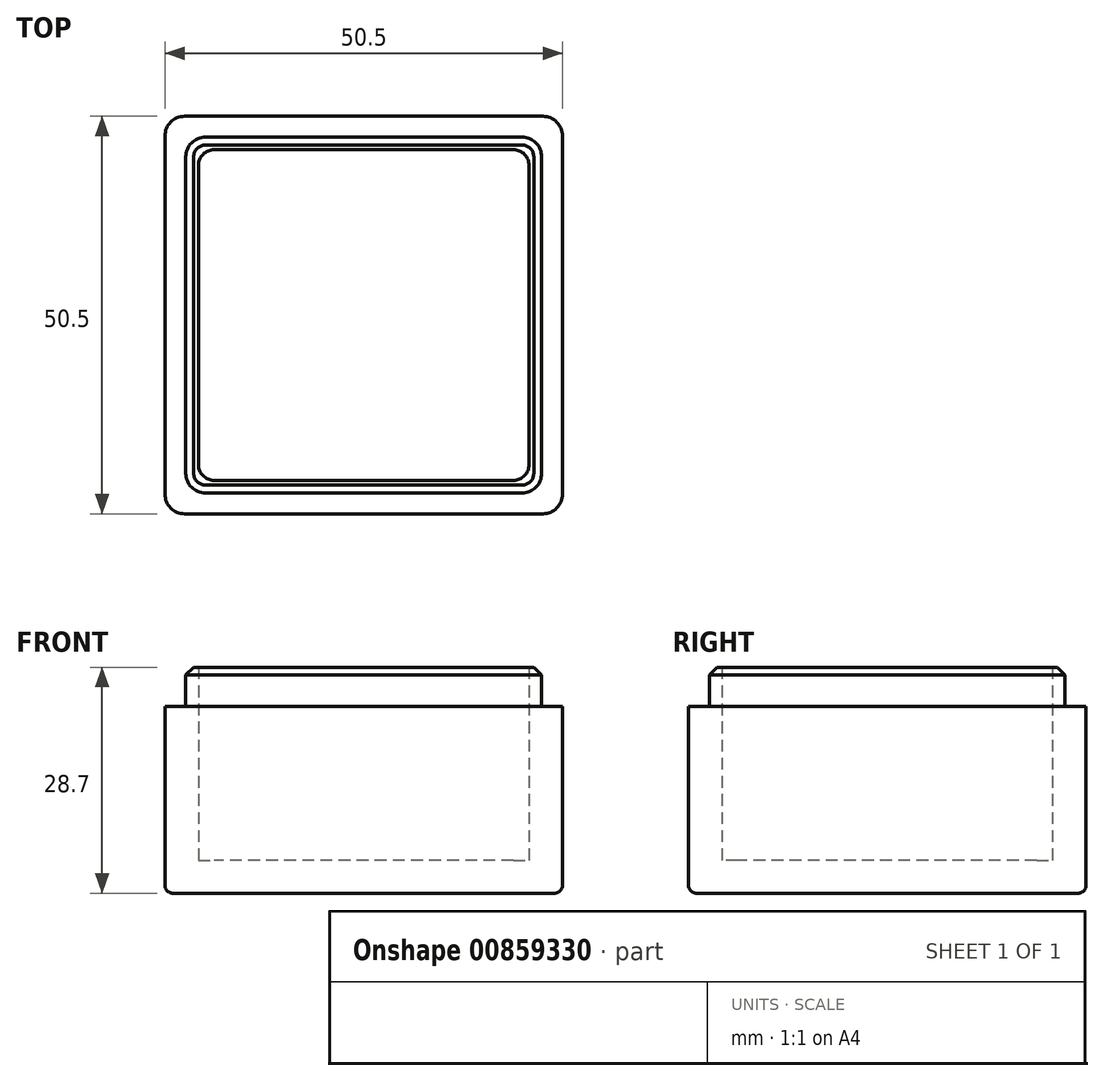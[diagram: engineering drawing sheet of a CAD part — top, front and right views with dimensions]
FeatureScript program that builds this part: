
annotation { "Feature Type Name" : "Feature", "Feature Type Description" : "" }
export const myFeature = defineFeature(function(context is Context, id is Id, definition is map)
    precondition{}
    {
        {
            var Q0;
            Q0=qCreatedBy(makeId("Top.planeOp"),FACE);
            var sketch = newSketch(context, id + "F0", { "sketchPlane" : qUnion([Q0])});
            skLineSegment(sketch, "E0.bottom", {"start": v(25.25, 25.25) * mm, "end": v(-25.25, 25.25) * mm});
            skLineSegment(sketch, "E0.top", {"start": v(25.25, -25.25) * mm, "end": v(-25.25, -25.25) * mm});
            skLineSegment(sketch, "E0.left", {"start": v(25.25, 25.25) * mm, "end": v(25.25, -25.25) * mm});
            skLineSegment(sketch, "E0.right", {"start": v(-25.25, 25.25) * mm, "end": v(-25.25, -25.25) * mm});
            skPoint(sketch, "E0.middle", {"position": v(0, 0) * mm});
            skSolve(sketch);
        }
        {
            var Q0;
            Q0=qSketchRegion(id+"F0",true);
            extrude(context, id + "F1", {"entities" : qUnion([Q0]), "depth" : (2 + 20 + 1.7) * mm, "offsetDistance" : 25 * mm});
        }
        {
            var Q0;
            Q0=makeQuery(id+"F1.opExtrude","CAP_FACE",FACE,{"disambiguationData":[OSD([sQuery(id+"F0.wireOp",EDGE,"E0.bottom"),sQuery(id+"F0.wireOp",EDGE,"E0.top"),sQuery(id+"F0.wireOp",EDGE,"E0.left"),sQuery(id+"F0.wireOp",EDGE,"E0.right")])],"isStart":false});
            var sketch = newSketch(context, id + "F2", { "sketchPlane" : qUnion([Q0])});
            skLineSegment(sketch, "E1.bottom", {"start": v(22.6, 22.6) * mm, "end": v(-22.6, 22.6) * mm});
            skLineSegment(sketch, "E1.top", {"start": v(22.6, -22.6) * mm, "end": v(-22.6, -22.6) * mm});
            skLineSegment(sketch, "E1.left", {"start": v(22.6, 22.6) * mm, "end": v(22.6, -22.6) * mm});
            skLineSegment(sketch, "E1.right", {"start": v(-22.6, 22.6) * mm, "end": v(-22.6, -22.6) * mm});
            skPoint(sketch, "E1.middle", {"position": v(0, 0) * mm});
            skSolve(sketch);
        }
        {
            var Q0;
            Q0=qSketchRegion(id+"F2",true);
            extrude(context, id + "F3", {"entities" : qUnion([Q0]), "operationType" : NewBodyOperationType.ADD, "depth" : 5 * mm, "offsetDistance" : 25 * mm});
        }
        {
            var Q0;
            Q0=makeQuery(id+"F1.opExtrude","CAP_FACE",FACE,{"disambiguationData":[OSD([sQuery(id+"F0.wireOp",EDGE,"E0.bottom"),sQuery(id+"F0.wireOp",EDGE,"E0.top"),sQuery(id+"F0.wireOp",EDGE,"E0.left"),sQuery(id+"F0.wireOp",EDGE,"E0.right")])],"isStart":false});
            var sketch = newSketch(context, id + "F4", { "sketchPlane" : qUnion([Q0])});
            skLineSegment(sketch, "E2.bottom", {"start": v(21, 21) * mm, "end": v(-21, 21) * mm});
            skLineSegment(sketch, "E2.top", {"start": v(21, -21) * mm, "end": v(-21, -21) * mm});
            skLineSegment(sketch, "E2.left", {"start": v(21, 21) * mm, "end": v(21, -21) * mm});
            skLineSegment(sketch, "E2.right", {"start": v(-21, 21) * mm, "end": v(-21, -21) * mm});
            skPoint(sketch, "E2.middle", {"position": v(0, 0) * mm});
            skSolve(sketch);
        }
        {
            var Q0;
            Q0=qSketchRegion(id+"F4",true);
            extrude(context, id + "F5", {"entities" : qUnion([Q0]), "operationType" : NewBodyOperationType.REMOVE, "endBound" : BoundingType.UP_TO_NEXT, "depth" : 25 * mm, "offsetDistance" : 25 * mm, "hasSecondDirection" : true, "secondDirectionOppositeDirection" : true, "secondDirectionDepth" : 19.5 * mm});
        }
        {
            var Q0;
            Q0=makeQuery(id+"F1.opExtrude","SWEPT_EDGE",EDGE,{"disambiguationData":[OSD([sQuery(id+"F0.wireOp",EDGE,"E0.bottom"),sQuery(id+"F0.wireOp",EDGE,"E0.right")])]});
            var Q1;
            Q1=makeQuery(id+"F1.opExtrude","SWEPT_EDGE",EDGE,{"disambiguationData":[OSD([sQuery(id+"F0.wireOp",EDGE,"E0.top"),sQuery(id+"F0.wireOp",EDGE,"E0.right")])]});
            var Q2;
            Q2=makeQuery(id+"F1.opExtrude","SWEPT_EDGE",EDGE,{"disambiguationData":[OSD([sQuery(id+"F0.wireOp",EDGE,"E0.top"),sQuery(id+"F0.wireOp",EDGE,"E0.left")])]});
            var Q3;
            Q3=makeQuery(id+"F1.opExtrude","SWEPT_EDGE",EDGE,{"disambiguationData":[OSD([sQuery(id+"F0.wireOp",EDGE,"E0.bottom"),sQuery(id+"F0.wireOp",EDGE,"E0.left")])]});
            var Q4;
            Q4=makeQuery(id+"F3.opExtrude","SWEPT_EDGE",EDGE,{"disambiguationData":[OSD([sQuery(id+"F2.wireOp",EDGE,"E1.bottom"),sQuery(id+"F2.wireOp",EDGE,"E1.right")])]});
            var Q5;
            Q5=makeQuery(id+"F3.opExtrude","SWEPT_EDGE",EDGE,{"disambiguationData":[OSD([sQuery(id+"F2.wireOp",EDGE,"E1.top"),sQuery(id+"F2.wireOp",EDGE,"E1.right")])]});
            var Q6;
            Q6=makeQuery(id+"F3.opExtrude","SWEPT_EDGE",EDGE,{"disambiguationData":[OSD([sQuery(id+"F2.wireOp",EDGE,"E1.top"),sQuery(id+"F2.wireOp",EDGE,"E1.left")])]});
            var Q7;
            Q7=makeQuery(id+"F3.opExtrude","SWEPT_EDGE",EDGE,{"disambiguationData":[OSD([sQuery(id+"F2.wireOp",EDGE,"E1.bottom"),sQuery(id+"F2.wireOp",EDGE,"E1.left")])]});
            fillet(context, id + "F6", {"entities" : qUnion([Q0, Q1, Q2, Q3, Q4, Q5, Q6, Q7]), "radius" : 2.5 * mm, "tangentPropagation" : true, "allowEdgeOverflow" : false});
        }
        {
            var Q0;
            Q0=makeQuery(id+"F5.boolean.opBoolean","COPY",EDGE,{"derivedFrom":makeQuery(id+"F5.opExtrude","SWEPT_EDGE",EDGE,{"disambiguationData":[OSD([sQuery(id+"F4.wireOp",EDGE,"E2.bottom"),sQuery(id+"F4.wireOp",EDGE,"E2.right")])]})});
            var Q1;
            Q1=makeQuery(id+"F5.boolean.opBoolean","COPY",EDGE,{"derivedFrom":makeQuery(id+"F5.opExtrude","SWEPT_EDGE",EDGE,{"disambiguationData":[OSD([sQuery(id+"F4.wireOp",EDGE,"E2.bottom"),sQuery(id+"F4.wireOp",EDGE,"E2.left")])]})});
            var Q2;
            Q2=makeQuery(id+"F5.boolean.opBoolean","COPY",EDGE,{"derivedFrom":makeQuery(id+"F5.opExtrude","SWEPT_EDGE",EDGE,{"disambiguationData":[OSD([sQuery(id+"F4.wireOp",EDGE,"E2.top"),sQuery(id+"F4.wireOp",EDGE,"E2.left")])]})});
            var Q3;
            Q3=makeQuery(id+"F5.boolean.opBoolean","COPY",EDGE,{"derivedFrom":makeQuery(id+"F5.opExtrude","SWEPT_EDGE",EDGE,{"disambiguationData":[OSD([sQuery(id+"F4.wireOp",EDGE,"E2.top"),sQuery(id+"F4.wireOp",EDGE,"E2.right")])]})});
            fillet(context, id + "F7", {"entities" : qUnion([Q0, Q1, Q2, Q3]), "radius" : 2 * mm, "tangentPropagation" : true, "allowEdgeOverflow" : false});
        }
        {
            var Q0;
            Q0=makeQuery(id+"F3.opExtrude","CAP_EDGE",EDGE,{"disambiguationData":[OSD([sQuery(id+"F2.wireOp",EDGE,"E1.right")])],"isStart":false});
            chamfer(context, id + "F8", {"entities" : qUnion([Q0]), "width" : 1 * mm, "tangentPropagation" : true});
        }
        {
            var Q0;
            Q0=makeQuery(id+"F1.opExtrude","CAP_EDGE",EDGE,{"disambiguationData":[OSD([sQuery(id+"F0.wireOp",EDGE,"E0.bottom")])],"isStart":true});
            fillet(context, id + "F9", {"entities" : qUnion([Q0]), "radius" : 1 * mm, "tangentPropagation" : true, "allowEdgeOverflow" : false});
        }
    });
